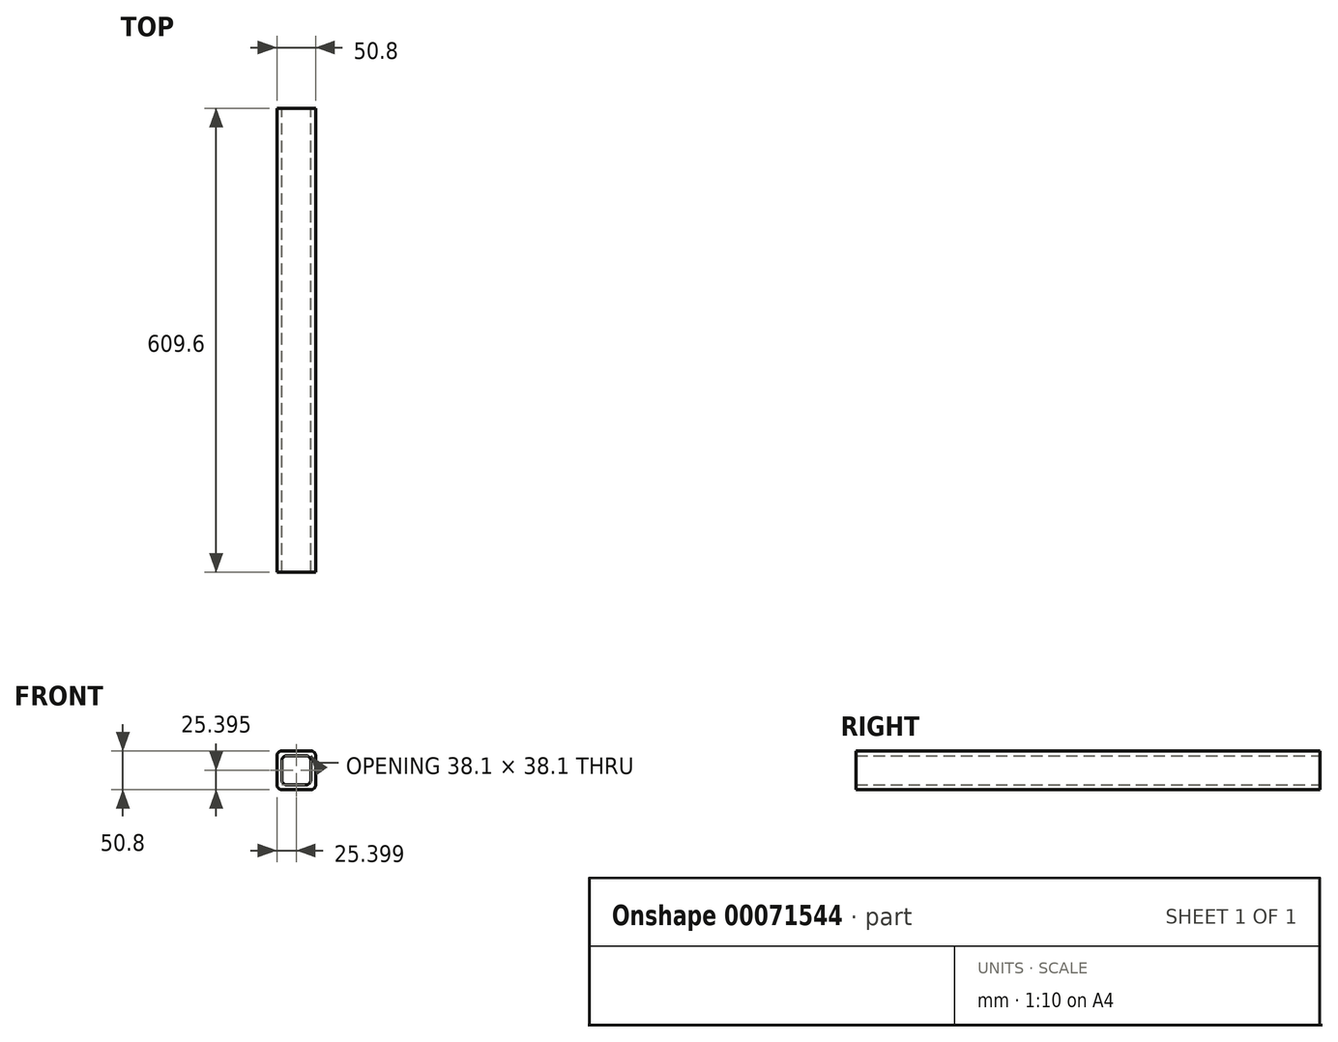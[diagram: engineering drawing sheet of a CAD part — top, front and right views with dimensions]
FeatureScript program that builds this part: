
annotation { "Feature Type Name" : "Feature", "Feature Type Description" : "" }
export const myFeature = defineFeature(function(context is Context, id is Id, definition is map)
    precondition{}
    {
        {
            var Q0;
            Q0=qCreatedBy(makeId("Front.planeOp"),FACE);
            var sketch = newSketch(context, id + "F0", { "sketchPlane" : qUnion([Q0])});
            skLineSegment(sketch, "E0.bottom", {"start": v(-15.57, 26.83) * mm, "end": v(22.53, 26.83) * mm});
            skLineSegment(sketch, "E0.top", {"start": v(-15.57, -23.97) * mm, "end": v(22.53, -23.97) * mm});
            skLineSegment(sketch, "E0.left", {"start": v(-21.92, 20.48) * mm, "end": v(-21.92, -17.62) * mm});
            skLineSegment(sketch, "E0.right", {"start": v(28.88, 20.48) * mm, "end": v(28.88, -17.62) * mm});
            skLineSegment(sketch, "E1.bottom", {"start": v(-9.22, 20.48) * mm, "end": v(16.18, 20.48) * mm});
            skLineSegment(sketch, "E1.top", {"start": v(-9.22, -17.62) * mm, "end": v(16.18, -17.62) * mm});
            skLineSegment(sketch, "E1.left", {"start": v(-15.57, 14.13) * mm, "end": v(-15.57, -11.27) * mm});
            skLineSegment(sketch, "E1.right", {"start": v(22.53, 14.13) * mm, "end": v(22.53, -11.27) * mm});
            skPoint(sketch, "E2.visualSharp", {"position": v(-15.57, 20.48) * mm});
            skArc(sketch, "E2.filletArc", {"start": v(-9.22, 20.48) * mm, "mid": v(-13.71, 18.62) * mm, "end": v(-15.57, 14.13) * mm});
            skPoint(sketch, "E3.visualSharp", {"position": v(22.53, 20.48) * mm});
            skArc(sketch, "E3.filletArc", {"start": v(22.53, 14.13) * mm, "mid": v(20.67, 18.62) * mm, "end": v(16.18, 20.48) * mm});
            skPoint(sketch, "E4.visualSharp", {"position": v(22.53, -17.62) * mm});
            skArc(sketch, "E4.filletArc", {"start": v(16.18, -17.62) * mm, "mid": v(20.67, -15.76) * mm, "end": v(22.53, -11.27) * mm});
            skPoint(sketch, "E5.visualSharp", {"position": v(-15.57, -17.62) * mm});
            skArc(sketch, "E5.filletArc", {"start": v(-15.57, -11.27) * mm, "mid": v(-13.71, -15.76) * mm, "end": v(-9.22, -17.62) * mm});
            skPoint(sketch, "E6.visualSharp", {"position": v(-21.92, 26.83) * mm});
            skArc(sketch, "E6.filletArc", {"start": v(-15.57, 26.83) * mm, "mid": v(-20.06, 24.97) * mm, "end": v(-21.92, 20.48) * mm});
            skPoint(sketch, "E7.visualSharp", {"position": v(28.88, 26.83) * mm});
            skArc(sketch, "E7.filletArc", {"start": v(28.88, 20.48) * mm, "mid": v(27.02, 24.97) * mm, "end": v(22.53, 26.83) * mm});
            skPoint(sketch, "E8.visualSharp", {"position": v(28.88, -23.97) * mm});
            skArc(sketch, "E8.filletArc", {"start": v(22.53, -23.97) * mm, "mid": v(27.02, -22.11) * mm, "end": v(28.88, -17.62) * mm});
            skPoint(sketch, "E9.visualSharp", {"position": v(-21.92, -23.97) * mm});
            skArc(sketch, "E9.filletArc", {"start": v(-21.92, -17.62) * mm, "mid": v(-20.06, -22.11) * mm, "end": v(-15.57, -23.97) * mm});
            skSolve(sketch);
        }
        {
            var Q0;
            Q0 = qSketchRegion(id + "F0", true);
            extrude(context, id + "F1", {"entities" : qUnion([Q0]), "depth" : 609.6 * mm});
        }
    });
